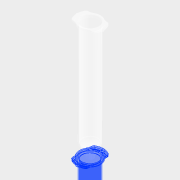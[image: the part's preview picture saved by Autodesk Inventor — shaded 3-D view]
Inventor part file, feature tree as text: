
AUTODESK INVENTOR PART (.ipt)
format: ipt  version: 2019.3 (Build 233278000, 278)  size: 1,835,008 bytes
history: native  units: in
note: dims shown in document units (in); Inventor stores cm internally (conversion verified against a paired STEP export)
features: sketch x2, imported_body x1, revolve x1
ambient origin geometry x8: Origin, YZ Plane, XZ Plane, XY Plane, X Axis, Y Axis, Z Axis, Center Point
bodies: Solid1 (feature_tree), Solid2 (feature_tree)
feature tree (4):
  imported_body  "Imported1"
  sketch  "Sketch1"  dims[d1=0.0019in d2=5.9309in]
  revolve  "Revolution1"  [1 undecoded]
  sketch  "Sketch3"  dims[d3=1.0261in d5=6.691in d6=0.9979in d7=1.0263in d8=0.2795in d9=0.1565in d10=0.1734in d11=0.0234in d12=0.284in d13=90.0deg]
note: 1 required parameter value undecoded (feature->parameter linkage not recoverable at this tier; creation-order binding heuristic only, values carry confidence <= 0.55)
